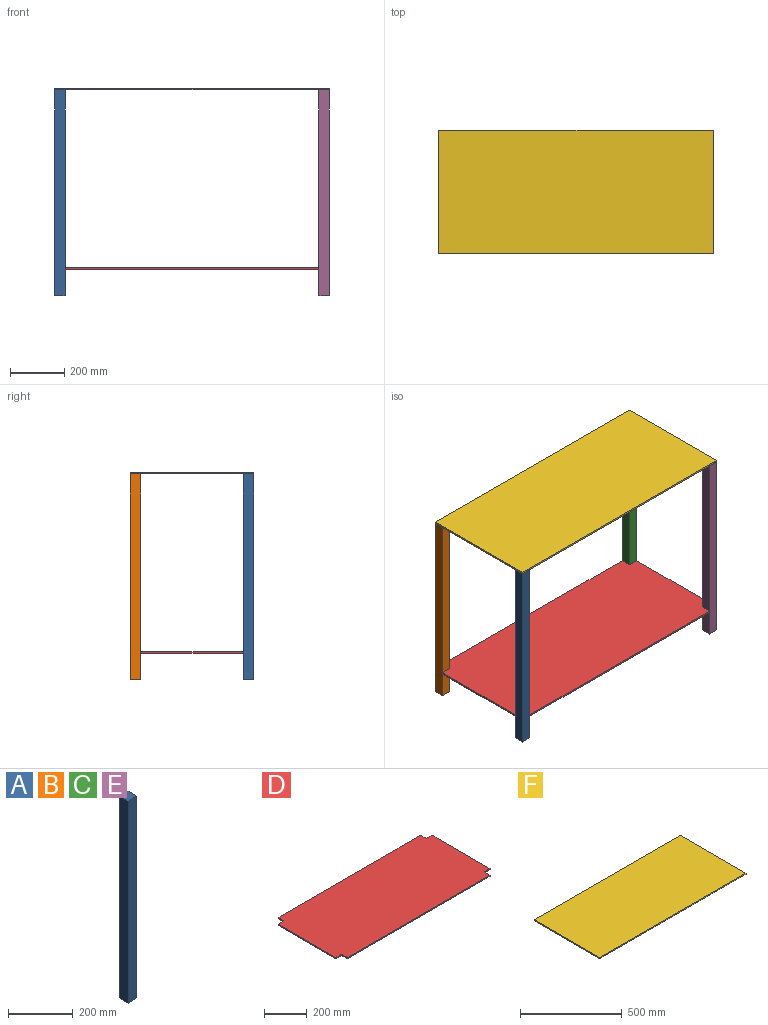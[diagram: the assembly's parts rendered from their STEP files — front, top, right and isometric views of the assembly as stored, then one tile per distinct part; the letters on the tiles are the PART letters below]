
ASSEMBLY  parts=6 mates=5
PART A: 6 faces, bbox 38.1x38.1x762 mm
  f0: plane 762x38.1mm, normal (0,-1,0), area 29032.2mm2, adj f1,f3,f4,f5
  f1: plane 762x38.1mm, normal (1,0,0), area 29032.2mm2, adj f0,f2,f4,f5
  f2: plane 762x38.1mm, normal (0,1,0), area 29032.2mm2, adj f1,f3,f4,f5
  f3: plane 762x38.1mm, normal (-1,0,0), area 29032.2mm2, adj f0,f2,f4,f5
  f4: plane 38.1x38.1mm, normal (0,0,1), area 1451.6mm2, adj f0,f1,f2,f3
  f5: plane 38.1x38.1mm, normal (0,0,-1), area 1451.6mm2, adj f0,f1,f2,f3
PART B: same geometry as A
PART C: same geometry as A
PART D: 14 faces, bbox 1016x457.2x6.4 mm
  f0: plane 381x6.35mm, normal (-1,0,0), area 2419.3mm2, adj f1,f11,f12,f13
  f1: plane 38.1x6.35mm, normal (0,-1,0), area 241.9mm2, adj f0,f2,f12,f13
  f2: plane 38.1x6.35mm, normal (-1,0,0), area 241.9mm2, adj f1,f3,f12,f13
  f3: plane 939.8x6.35mm, normal (0,-1,0), area 5967.7mm2, adj f2,f4,f12,f13
  f4: plane 38.1x6.35mm, normal (1,0,0), area 241.9mm2, adj f3,f5,f12,f13
  f5: plane 38.1x6.35mm, normal (0,-1,0), area 241.9mm2, adj f4,f6,f12,f13
  f6: plane 381x6.35mm, normal (1,0,0), area 2419.3mm2, adj f5,f7,f12,f13
  f7: plane 38.1x6.35mm, normal (0,1,0), area 241.9mm2, adj f6,f8,f12,f13
  f8: plane 38.1x6.35mm, normal (1,0,0), area 241.9mm2, adj f7,f9,f12,f13
  f9: plane 939.8x6.35mm, normal (0,1,0), area 5967.7mm2, adj f8,f10,f12,f13
  f10: plane 38.1x6.35mm, normal (-1,0,0), area 241.9mm2, adj f9,f11,f12,f13
  f11: plane 38.1x6.35mm, normal (0,1,0), area 241.9mm2, adj f0,f10,f12,f13
  f12: plane 1016x457.2mm, normal (0,0,1), area 458708.8mm2, adj f0,f1,f2,f3,f4,f5,f6,f7
  f13: plane 1016x457.2mm, normal (0,0,-1), area 458708.8mm2, adj f0,f1,f2,f3,f4,f5,f6,f7
PART E: same geometry as A
PART F: 6 faces, bbox 1016x457.2x6.4 mm
  f0: plane 1016x6.35mm, normal (0,-1,0), area 6451.6mm2, adj f1,f3,f4,f5
  f1: plane 457.2x6.35mm, normal (1,0,0), area 2903.2mm2, adj f0,f2,f4,f5
  f2: plane 1016x6.35mm, normal (0,1,0), area 6451.6mm2, adj f1,f3,f4,f5
  f3: plane 457.2x6.35mm, normal (-1,0,0), area 2903.2mm2, adj f0,f2,f4,f5
  f4: plane 1016x457.2mm, normal (0,0,1), area 464515.2mm2, adj f0,f1,f2,f3
  f5: plane 1016x457.2mm, normal (0,0,-1), area 464515.2mm2, adj f0,f1,f2,f3
PLACE A rot(axis=(1,0,0),180deg) t=(-488.95,-209.55,279.92)mm
PLACE B rot(axis=(1,0,0),180deg) t=(-488.95,209.55,279.92)mm
PLACE C rot(axis=(1,0,0),180deg) t=(488.95,209.55,279.92)mm
PLACE D at identity fixed
PLACE E rot(axis=(1,0,0),180deg) t=(488.95,-209.55,279.92)mm
PLACE F t=(0,0,660.92)mm
MATE planar A.f0 <-> D.f1  axis (0,1,0) through (-488.95,-190.5,279.92)mm
MATE planar F.f5 <-> A.f5  axis (0,0,-1) through (0,0,660.92)mm
MATE planar A.f1 <-> D.f2  axis (1,0,0) through (-469.9,-209.55,279.92)mm
MATE planar F.f0 <-> E.f2  axis (0,-1,0) through (0,-228.6,664.1)mm
MATE planar F.f1 <-> C.f1  axis (1,0,0) through (508,0,664.1)mm
